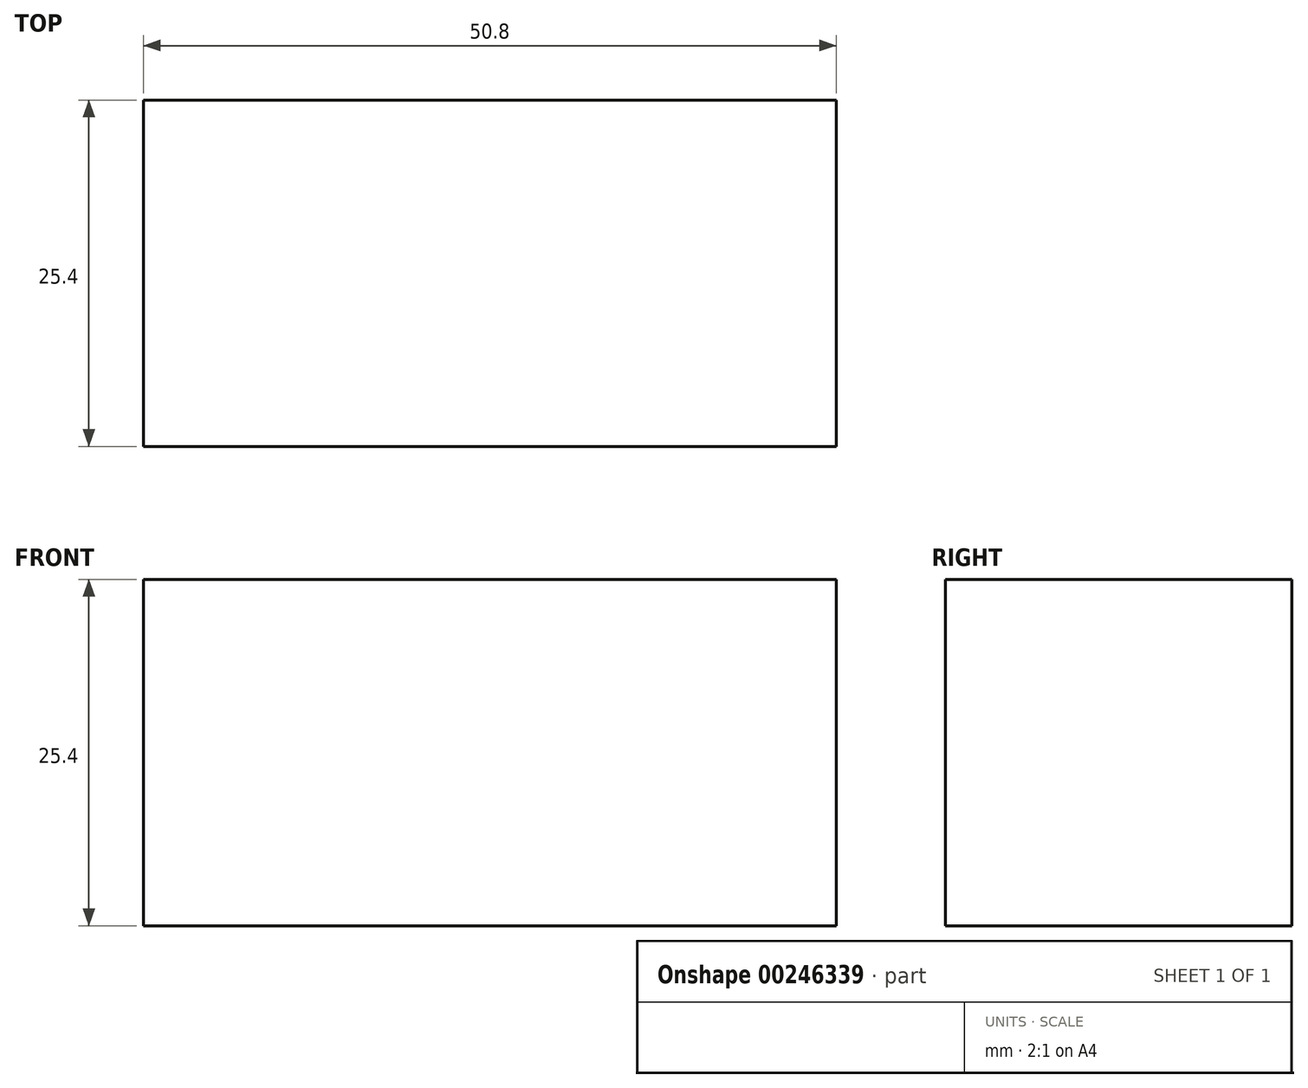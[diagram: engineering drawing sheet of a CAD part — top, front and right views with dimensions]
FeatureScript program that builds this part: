
annotation { "Feature Type Name" : "Feature", "Feature Type Description" : "" }
export const myFeature = defineFeature(function(context is Context, id is Id, definition is map)
    precondition{}
    {
        {
            var Q0;
            Q0=qCreatedBy(makeId("Front.planeOp"),FACE);
            var sketch = newSketch(context, id + "F0", { "sketchPlane" : qUnion([Q0])});
            skLineSegment(sketch, "E0.bottom", {"start": v(-25.4, 25.4) * mm, "end": v(25.4, 25.4) * mm});
            skLineSegment(sketch, "E0.top", {"start": v(-25.4, 0) * mm, "end": v(25.4, 0) * mm});
            skLineSegment(sketch, "E0.left", {"start": v(-25.4, 25.4) * mm, "end": v(-25.4, 0) * mm});
            skLineSegment(sketch, "E0.right", {"start": v(25.4, 25.4) * mm, "end": v(25.4, 0) * mm});
            skLineSegment(sketch, "E1.bottom", {"start": v(0, 0) * mm, "end": v(25.4, 0) * mm});
            skLineSegment(sketch, "E1.top", {"start": v(0, -25.4) * mm, "end": v(25.4, -25.4) * mm});
            skLineSegment(sketch, "E1.left", {"start": v(0, 0) * mm, "end": v(0, -25.4) * mm});
            skLineSegment(sketch, "E1.right", {"start": v(25.4, 0) * mm, "end": v(25.4, -25.4) * mm});
            skSolve(sketch);
        }
        {
            var Q0;
            Q0=makeQuery(id+"F0.imprint","IMPRINT",FACE,{"disambiguationData":[TD([[makeQuery(id+"F0.imprint","IMPRINT",EDGE,{"derivedFrom":sQuery(id+"F0.wireOp",EDGE,"E0.bottom")}),-1.0]])]});
            var Q1;
            Q1=makeQuery(id+"F0.imprint","IMPRINT",FACE,{"disambiguationData":[TD([[makeQuery(id+"F0.imprint","IMPRINT",EDGE,{"derivedFrom":sQuery(id+"F0.wireOp",EDGE,"E1.bottom")}),-1.0]])]});
            extrude(context, id + "F1", {"entities" : qUnion([Q0, Q1]), "depth" : 25.4 * mm});
        }
    });
